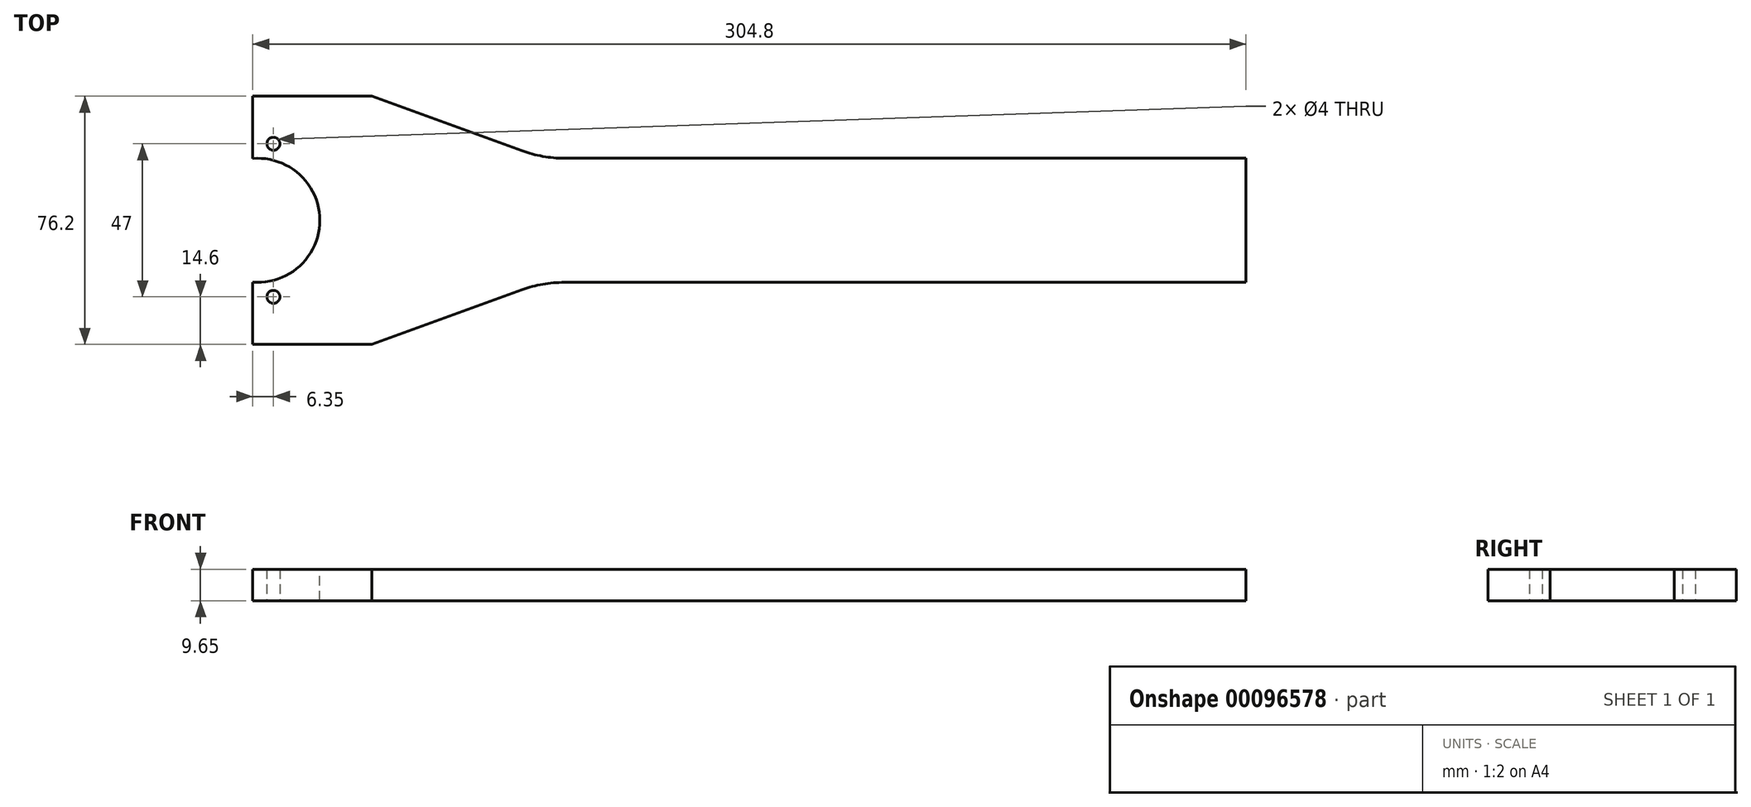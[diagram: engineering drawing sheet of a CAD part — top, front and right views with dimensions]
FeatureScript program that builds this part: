
annotation { "Feature Type Name" : "Feature", "Feature Type Description" : "" }
export const myFeature = defineFeature(function(context is Context, id is Id, definition is map)
    precondition{}
    {
        {
            var Q0;
            Q0=qCreatedBy(makeId("Top.planeOp"),FACE);
            var sketch = newSketch(context, id + "F0", { "sketchPlane" : qUnion([Q0])});
            skLineSegment(sketch, "E0.bottom", {"start": v(0, 0) * mm, "end": v(304.8, 0) * mm});
            skLineSegment(sketch, "E0.top", {"start": v(0, 76.2) * mm, "end": v(304.8, 76.2) * mm});
            skLineSegment(sketch, "E0.left", {"start": v(0, 0) * mm, "end": v(0, 76.2) * mm});
            skLineSegment(sketch, "E0.right", {"start": v(304.8, 0) * mm, "end": v(304.8, 76.2) * mm});
            skSolve(sketch);
        }
        {
            var Q0;
            Q0=makeQuery(id+"F0.imprint","IMPRINT",FACE,{"disambiguationData":[TD([[makeQuery(id+"F0.imprint","IMPRINT",EDGE,{"derivedFrom":sQuery(id+"F0.wireOp",EDGE,"E0.bottom")}),1.0]])]});
            extrude(context, id + "F1", {"entities" : qUnion([Q0]), "depth" : 9.65 * mm});
        }
        {
            var Q0;
            Q0=makeQuery(id+"F1.opExtrude","CAP_FACE",FACE,{"disambiguationData":[OSD([sQuery(id+"F0.wireOp",EDGE,"E0.bottom"),sQuery(id+"F0.wireOp",EDGE,"E0.top"),sQuery(id+"F0.wireOp",EDGE,"E0.left"),sQuery(id+"F0.wireOp",EDGE,"E0.right")])],"isStart":false});
            var sketch = newSketch(context, id + "F2", { "sketchPlane" : qUnion([Q0])});
            skCircle(sketch, "E1", {"center": v(1.52, 38.1) * mm, "radius": 19.05 * mm});
            skSolve(sketch);
        }
        {
            var Q0;
            {var subQ0=sQuery(id+"F2.wireOp",EDGE,"E1");var subQ1=makeQuery(id+"F1.opExtrude","CAP_EDGE",EDGE,{"disambiguationData":[OSD([sQuery(id+"F0.wireOp",EDGE,"E0.left")])],"isStart":false});var subQ2=makeQuery(id+"F2.imprint","INTERSECT",VERTEX,{"disambiguationData":[OD(0.0)],"derivedFrom":[subQ1,subQ0]});Q0=makeQuery(id+"F2.imprint","IMPRINT",FACE,{"disambiguationData":[TD([[makeQuery(id+"F2.imprint","IMPRINT",EDGE,{"disambiguationData":[TD([[subQ2,-1.0]])],"derivedFrom":subQ0}),1.0]])]});}
            extrude(context, id + "F3", {"entities" : qUnion([Q0]), "operationType" : NewBodyOperationType.REMOVE, "endBound" : BoundingType.THROUGH_ALL, "oppositeDirection" : true, "depth" : 25.4 * mm});
        }
        {
            var Q0;
            Q0=makeQuery(id+"F1.opExtrude","CAP_FACE",FACE,{"disambiguationData":[OSD([sQuery(id+"F0.wireOp",EDGE,"E0.bottom"),sQuery(id+"F0.wireOp",EDGE,"E0.top"),sQuery(id+"F0.wireOp",EDGE,"E0.left"),sQuery(id+"F0.wireOp",EDGE,"E0.right")])],"isStart":true});
            var sketch = newSketch(context, id + "F4", { "sketchPlane" : qUnion([Q0])});
            skLineSegment(sketch, "E2", {"start": v(36.56, 0) * mm, "end": v(82.59, -16.75) * mm});
            skLineSegment(sketch, "E3", {"start": v(95.62, -19.05) * mm, "end": v(304.8, -19.05) * mm});
            skLineSegment(sketch, "E4", {"start": v(304.8, -19.05) * mm, "end": v(304.8, -57.15) * mm});
            skLineSegment(sketch, "E5", {"start": v(304.8, -57.15) * mm, "end": v(95.62, -57.15) * mm});
            skLineSegment(sketch, "E6", {"start": v(82.59, -59.45) * mm, "end": v(36.56, -76.2) * mm});
            skPoint(sketch, "E7.visualSharp", {"position": v(88.9, -57.15) * mm});
            skArc(sketch, "E7.filletArc", {"start": v(95.62, -57.15) * mm, "mid": v(89, -57.73) * mm, "end": v(82.59, -59.45) * mm});
            skPoint(sketch, "E8.visualSharp", {"position": v(88.9, -19.05) * mm});
            skArc(sketch, "E8.filletArc", {"start": v(82.59, -16.75) * mm, "mid": v(89, -18.47) * mm, "end": v(95.62, -19.05) * mm});
            skSolve(sketch);
        }
        {
            var Q0;
            {var subQ0=sQuery(id+"F4.wireOp",EDGE,"E2");Q0=makeQuery(id+"F4.imprint","IMPRINT",FACE,{"disambiguationData":[TD([[makeQuery(id+"F4.imprint","IMPRINT",EDGE,{"derivedFrom":subQ0}),1.0]])]});}
            var Q1;
            {var subQ0=sQuery(id+"F4.wireOp",EDGE,"E5");Q1=makeQuery(id+"F4.imprint","IMPRINT",FACE,{"disambiguationData":[TD([[makeQuery(id+"F4.imprint","IMPRINT",EDGE,{"derivedFrom":subQ0}),1.0]])]});}
            extrude(context, id + "F5", {"entities" : qUnion([Q0, Q1]), "operationType" : NewBodyOperationType.REMOVE, "oppositeDirection" : true, "depth" : 25.4 * mm});
        }
        {
            var Q0;
            Q0=makeQuery(id+"F1.opExtrude","CAP_FACE",FACE,{"disambiguationData":[OSD([sQuery(id+"F0.wireOp",EDGE,"E0.bottom"),sQuery(id+"F0.wireOp",EDGE,"E0.top"),sQuery(id+"F0.wireOp",EDGE,"E0.left"),sQuery(id+"F0.wireOp",EDGE,"E0.right")])],"isStart":true});
            var sketch = newSketch(context, id + "F6", { "sketchPlane" : qUnion([Q0])});
            skPoint(sketch, "E9", {"position": v(6.35, -14.6) * mm});
            skPoint(sketch, "E10", {"position": v(6.35, -61.6) * mm});
            skLineSegment(sketch, "E11", {"start": v(304.8, -38.1) * mm, "end": v(-11.27, -38.1) * mm});
            skSolve(sketch);
        }
        {
            var Q0;
            Q0=sQuery(id+"F6.wireOp",VERTEX,"E9");
            var Q1;
            Q1=sQuery(id+"F6.wireOp",VERTEX,"E10");
            var Q2;
            Q2=makeQuery(id+"F1.opExtrude","SWEPT_BODY",BODY,{"disambiguationData":[OSD([sQuery(id+"F0.wireOp",EDGE,"E0.bottom"),sQuery(id+"F0.wireOp",EDGE,"E0.top"),sQuery(id+"F0.wireOp",EDGE,"E0.left"),sQuery(id+"F0.wireOp",EDGE,"E0.right")])]});
            hole(context, id + "F7", {"style" : HoleStyle.SIMPLE, "endStyle" : HoleEndStyle.THROUGH, "holeDiameter" : 4 * mm, "locations" : qUnion([Q0, Q1]), "scope" : qUnion([Q2]), "isTappedThrough" : true});
        }
    });
